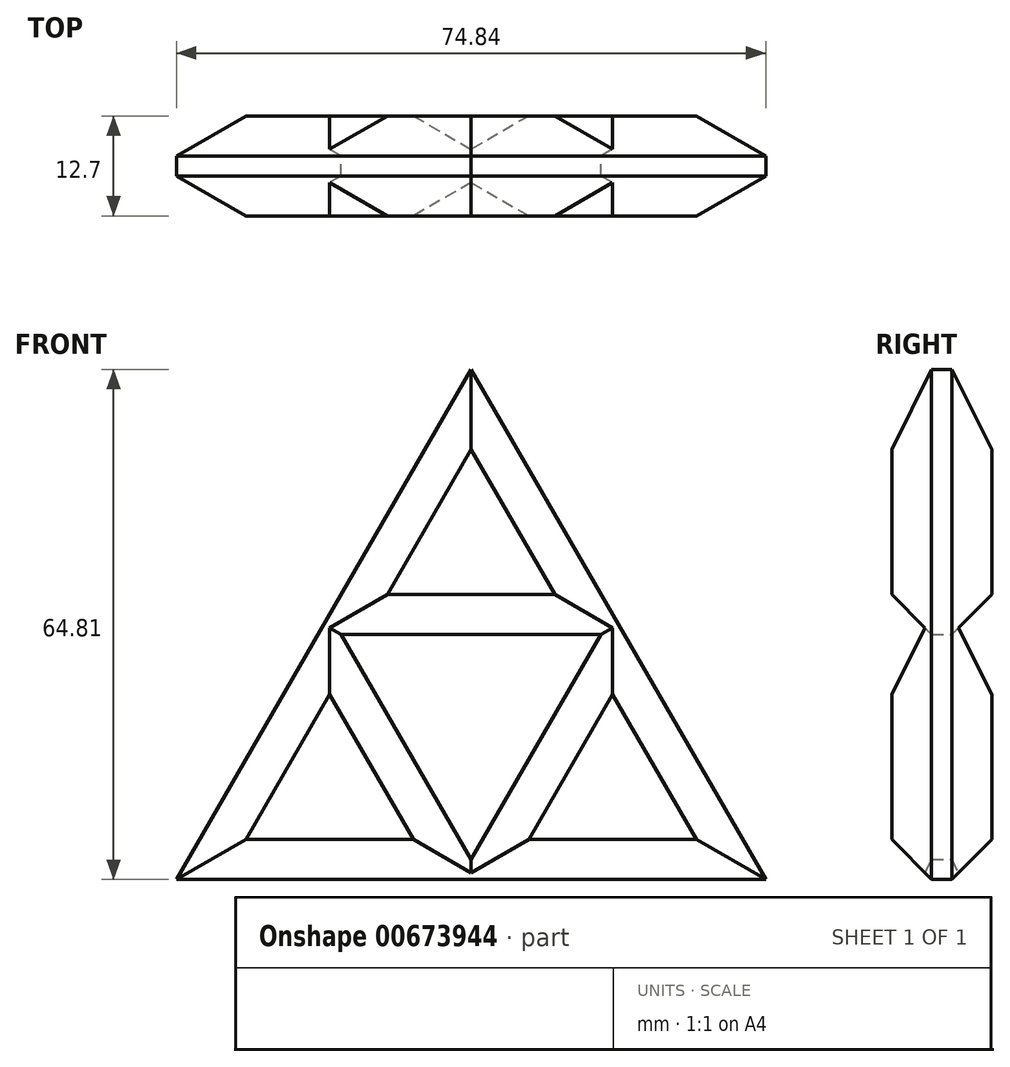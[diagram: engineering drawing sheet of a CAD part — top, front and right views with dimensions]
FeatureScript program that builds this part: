
annotation { "Feature Type Name" : "Feature", "Feature Type Description" : "" }
export const myFeature = defineFeature(function(context is Context, id is Id, definition is map)
    precondition{}
    {
        {
            var Q0;
            Q0=qCreatedBy(makeId("Front.planeOp"),FACE);
            var sketch = newSketch(context, id + "F0", { "sketchPlane" : qUnion([Q0])});
            skLineSegment(sketch, "E0", {"start": v(0, 0) * mm, "end": v(-33.02, 0) * mm});
            skLineSegment(sketch, "E1", {"start": v(-33.02, 0) * mm, "end": v(-16.51, 28.6) * mm});
            skLineSegment(sketch, "E2", {"start": v(-16.51, 28.6) * mm, "end": v(0, 0) * mm});
            skLineSegment(sketch, "E3", {"start": v(0, 0) * mm, "end": v(33.02, 0) * mm});
            skLineSegment(sketch, "E4", {"start": v(33.02, 0) * mm, "end": v(16.5, 28.6) * mm});
            skLineSegment(sketch, "E5", {"start": v(16.5, 28.6) * mm, "end": v(0, 0) * mm});
            skLineSegment(sketch, "E6", {"start": v(-16.51, 28.6) * mm, "end": v(16.5, 28.6) * mm});
            skLineSegment(sketch, "E7", {"start": v(16.51, 28.6) * mm, "end": v(0, 57.2) * mm});
            skLineSegment(sketch, "E8", {"start": v(0, 57.2) * mm, "end": v(-16.51, 28.6) * mm});
            skLineSegment(sketch, "E9", {"start": v(0, 57.2) * mm, "end": v(0, 62.27) * mm});
            skLineSegment(sketch, "E10", {"start": v(-33.02, 0) * mm, "end": v(-37.42, -2.54) * mm});
            skLineSegment(sketch, "E11", {"start": v(33.02, 0) * mm, "end": v(37.42, -2.54) * mm});
            skLineSegment(sketch, "E12", {"start": v(37.42, -2.54) * mm, "end": v(33.02, 0) * mm});
            skLineSegment(sketch, "E13", {"start": v(0, 62.27) * mm, "end": v(-37.42, -2.54) * mm});
            skLineSegment(sketch, "E14", {"start": v(-37.42, -2.54) * mm, "end": v(37.42, -2.54) * mm});
            skLineSegment(sketch, "E15", {"start": v(37.42, -2.54) * mm, "end": v(0, 62.27) * mm});
            skSolve(sketch);
        }
        {
            var Q0;
            Q0=makeQuery(id+"F0.imprint","IMPRINT",FACE,{"disambiguationData":[TD([[makeQuery(id+"F0.imprint","IMPRINT",EDGE,{"derivedFrom":sQuery(id+"F0.wireOp",EDGE,"E6")}),1.0]])]});
            var Q1;
            Q1=makeQuery(id+"F0.imprint","IMPRINT",FACE,{"disambiguationData":[TD([[makeQuery(id+"F0.imprint","IMPRINT",EDGE,{"derivedFrom":sQuery(id+"F0.wireOp",EDGE,"E0")}),-1.0]])]});
            var Q2;
            Q2=makeQuery(id+"F0.imprint","IMPRINT",FACE,{"disambiguationData":[TD([[makeQuery(id+"F0.imprint","IMPRINT",EDGE,{"derivedFrom":sQuery(id+"F0.wireOp",EDGE,"E3")}),1.0]])]});
            var Q3;
            Q3=makeQuery(id+"F0.imprint","IMPRINT",FACE,{"disambiguationData":[TD([[makeQuery(id+"F0.imprint","IMPRINT",EDGE,{"derivedFrom":sQuery(id+"F0.wireOp",EDGE,"E1")}),1.0]])]});
            var Q4;
            Q4=makeQuery(id+"F0.imprint","IMPRINT",FACE,{"disambiguationData":[TD([[makeQuery(id+"F0.imprint","IMPRINT",EDGE,{"derivedFrom":sQuery(id+"F0.wireOp",EDGE,"E4")}),-1.0]])]});
            var Q5;
            Q5=makeQuery(id+"F0.imprint","IMPRINT",FACE,{"disambiguationData":[TD([[makeQuery(id+"F0.imprint","IMPRINT",EDGE,{"derivedFrom":sQuery(id+"F0.wireOp",EDGE,"E0")}),1.0]])]});
            extrude(context, id + "F1", {"entities" : qUnion([Q0, Q1, Q2, Q3, Q4, Q5]), "depth" : 12.7 * mm});
        }
        {
            var Q0;
            Q0=makeQuery(id+"F1.opExtrude","CAP_EDGE",EDGE,{"disambiguationData":[OSD([sQuery(id+"F0.wireOp",EDGE,"E13")])],"isStart":false});
            var Q1;
            Q1=makeQuery(id+"F1.opExtrude","CAP_EDGE",EDGE,{"disambiguationData":[OSD([sQuery(id+"F0.wireOp",EDGE,"E2")])],"isStart":false});
            var Q2;
            Q2=makeQuery(id+"F1.opExtrude","CAP_EDGE",EDGE,{"disambiguationData":[OSD([sQuery(id+"F0.wireOp",EDGE,"E6")])],"isStart":false});
            var Q3;
            Q3=makeQuery(id+"F1.opExtrude","CAP_EDGE",EDGE,{"disambiguationData":[OSD([sQuery(id+"F0.wireOp",EDGE,"E5")])],"isStart":false});
            var Q4;
            Q4=makeQuery(id+"F1.opExtrude","CAP_EDGE",EDGE,{"disambiguationData":[OSD([sQuery(id+"F0.wireOp",EDGE,"E15")])],"isStart":false});
            var Q5;
            Q5=makeQuery(id+"F1.opExtrude","CAP_FACE",FACE,{"disambiguationData":[OSD([sQuery(id+"F0.wireOp",EDGE,"E2"),sQuery(id+"F0.wireOp",EDGE,"E5"),sQuery(id+"F0.wireOp",EDGE,"E6"),sQuery(id+"F0.wireOp",EDGE,"E13"),sQuery(id+"F0.wireOp",EDGE,"E14"),sQuery(id+"F0.wireOp",EDGE,"E15")])],"isStart":false});
            var Q6;
            Q6=makeQuery(id+"F1.opExtrude","CAP_EDGE",EDGE,{"disambiguationData":[OSD([sQuery(id+"F0.wireOp",EDGE,"E13")])],"isStart":true});
            var Q7;
            Q7=makeQuery(id+"F1.opExtrude","CAP_EDGE",EDGE,{"disambiguationData":[OSD([sQuery(id+"F0.wireOp",EDGE,"E15")])],"isStart":true});
            var Q8;
            Q8=makeQuery(id+"F1.opExtrude","CAP_EDGE",EDGE,{"disambiguationData":[OSD([sQuery(id+"F0.wireOp",EDGE,"E14")])],"isStart":true});
            var Q9;
            Q9=makeQuery(id+"F1.opExtrude","CAP_EDGE",EDGE,{"disambiguationData":[OSD([sQuery(id+"F0.wireOp",EDGE,"E5")])],"isStart":true});
            var Q10;
            Q10=makeQuery(id+"F1.opExtrude","CAP_EDGE",EDGE,{"disambiguationData":[OSD([sQuery(id+"F0.wireOp",EDGE,"E6")])],"isStart":true});
            var Q11;
            Q11=makeQuery(id+"F1.opExtrude","CAP_EDGE",EDGE,{"disambiguationData":[OSD([sQuery(id+"F0.wireOp",EDGE,"E2")])],"isStart":true});
            chamfer(context, id + "F2", {"entities" : qUnion([Q0, Q1, Q2, Q3, Q4, Q5, Q6, Q7, Q8, Q9, Q10, Q11]), "width" : 5.08 * mm, "tangentPropagation" : true});
        }
        {
            var Q0;
            Q0=makeQuery(id+"F2.opChamfer","SPLIT",FACE,{"disambiguationData":[OD(0.0)],"derivedFrom":makeQuery(id+"F1.opExtrude","CAP_FACE",FACE,{"disambiguationData":[OSD([sQuery(id+"F0.wireOp",EDGE,"E2"),sQuery(id+"F0.wireOp",EDGE,"E5"),sQuery(id+"F0.wireOp",EDGE,"E6"),sQuery(id+"F0.wireOp",EDGE,"E13"),sQuery(id+"F0.wireOp",EDGE,"E14"),sQuery(id+"F0.wireOp",EDGE,"E15")])],"isStart":false})});
            var Q1;
            {var subQ0=sQuery(id+"F0.wireOp",EDGE,"E2");Q1=makeQuery(id+"F2.opChamfer","BLEND_FACE",FACE,{"disambiguationData":[OSD([subQ0]),TDD([makeQuery(id+"F1.opExtrude","CAP_EDGE",EDGE,{"disambiguationData":[OSD([subQ0])],"isStart":false})])]});}
            var Q2;
            {var subQ0=sQuery(id+"F0.wireOp",EDGE,"E6");Q2=makeQuery(id+"F2.opChamfer","BLEND_FACE",FACE,{"disambiguationData":[OSD([subQ0]),TDD([makeQuery(id+"F1.opExtrude","CAP_EDGE",EDGE,{"disambiguationData":[OSD([subQ0])],"isStart":false})])]});}
            var Q3;
            Q3=makeQuery(id+"F2.opChamfer","SPLIT",FACE,{"disambiguationData":[OD(2.0)],"derivedFrom":makeQuery(id+"F1.opExtrude","CAP_FACE",FACE,{"disambiguationData":[OSD([sQuery(id+"F0.wireOp",EDGE,"E2"),sQuery(id+"F0.wireOp",EDGE,"E5"),sQuery(id+"F0.wireOp",EDGE,"E6"),sQuery(id+"F0.wireOp",EDGE,"E13"),sQuery(id+"F0.wireOp",EDGE,"E14"),sQuery(id+"F0.wireOp",EDGE,"E15")])],"isStart":false})});
            var Q4;
            {var subQ0=sQuery(id+"F0.wireOp",EDGE,"E5");Q4=makeQuery(id+"F2.opChamfer","BLEND_FACE",FACE,{"disambiguationData":[OSD([subQ0]),TDD([makeQuery(id+"F1.opExtrude","CAP_EDGE",EDGE,{"disambiguationData":[OSD([subQ0])],"isStart":false})])]});}
            var Q5;
            Q5=makeQuery(id+"F2.opChamfer","SPLIT",FACE,{"disambiguationData":[OD(1.0)],"derivedFrom":makeQuery(id+"F1.opExtrude","CAP_FACE",FACE,{"disambiguationData":[OSD([sQuery(id+"F0.wireOp",EDGE,"E2"),sQuery(id+"F0.wireOp",EDGE,"E5"),sQuery(id+"F0.wireOp",EDGE,"E6"),sQuery(id+"F0.wireOp",EDGE,"E13"),sQuery(id+"F0.wireOp",EDGE,"E14"),sQuery(id+"F0.wireOp",EDGE,"E15")])],"isStart":false})});
            var Q6;
            {var subQ0=sQuery(id+"F0.wireOp",EDGE,"E14");Q6=makeQuery(id+"F2.opChamfer","BLEND_FACE",FACE,{"disambiguationData":[OSD([subQ0]),TDD([makeQuery(id+"F1.opExtrude","CAP_EDGE",EDGE,{"disambiguationData":[OSD([subQ0])],"isStart":false})])]});}
            var Q7;
            {var subQ0=sQuery(id+"F0.wireOp",EDGE,"E15");Q7=makeQuery(id+"F2.opChamfer","BLEND_FACE",FACE,{"disambiguationData":[OSD([subQ0]),TDD([makeQuery(id+"F1.opExtrude","CAP_EDGE",EDGE,{"disambiguationData":[OSD([subQ0])],"isStart":false})])]});}
            var Q8;
            {var subQ0=sQuery(id+"F0.wireOp",EDGE,"E13");Q8=makeQuery(id+"F2.opChamfer","BLEND_FACE",FACE,{"disambiguationData":[OSD([subQ0]),TDD([makeQuery(id+"F1.opExtrude","CAP_EDGE",EDGE,{"disambiguationData":[OSD([subQ0])],"isStart":false})])]});}
            extrude(context, id + "F3", {"entities" : qUnion([Q0, Q1, Q2, Q3, Q4, Q5, Q6, Q7, Q8]), "operationType" : NewBodyOperationType.REMOVE, "oppositeDirection" : true, "depth" : 2.3 * mm});
        }
        {
            var Q0;
            {var subQ0=sQuery(id+"F0.wireOp",EDGE,"E15");var subQ1=sQuery(id+"F0.wireOp",EDGE,"E14");var subQ2=sQuery(id+"F0.wireOp",EDGE,"E13");var subQ3=sQuery(id+"F0.wireOp",EDGE,"E6");var subQ4=sQuery(id+"F0.wireOp",EDGE,"E5");var subQ5=sQuery(id+"F0.wireOp",EDGE,"E2");Q0=makeQuery(id+"F3.boolean.opBoolean","COPY",FACE,{"derivedFrom":makeQuery(id+"F3.opExtrude","CAP_FACE",FACE,{"disambiguationData":[OSD([subQ5,subQ4,subQ3,subQ2,subQ1,subQ0]),TDD([makeQuery(id+"F2.opChamfer","SPLIT",FACE,{"disambiguationData":[OD(0.0)],"derivedFrom":makeQuery(id+"F1.opExtrude","CAP_FACE",FACE,{"disambiguationData":[OSD([subQ5,subQ4,subQ3,subQ2,subQ1,subQ0])],"isStart":false})})])],"isStart":false})});}
            var Q1;
            {var subQ0=sQuery(id+"F0.wireOp",EDGE,"E15");var subQ1=sQuery(id+"F0.wireOp",EDGE,"E14");var subQ2=sQuery(id+"F0.wireOp",EDGE,"E13");var subQ3=sQuery(id+"F0.wireOp",EDGE,"E6");var subQ4=sQuery(id+"F0.wireOp",EDGE,"E5");var subQ5=sQuery(id+"F0.wireOp",EDGE,"E2");Q1=makeQuery(id+"F3.boolean.opBoolean","COPY",FACE,{"derivedFrom":makeQuery(id+"F3.opExtrude","CAP_FACE",FACE,{"disambiguationData":[OSD([subQ5,subQ4,subQ3,subQ2,subQ1,subQ0]),TDD([makeQuery(id+"F2.opChamfer","SPLIT",FACE,{"disambiguationData":[OD(2.0)],"derivedFrom":makeQuery(id+"F1.opExtrude","CAP_FACE",FACE,{"disambiguationData":[OSD([subQ5,subQ4,subQ3,subQ2,subQ1,subQ0])],"isStart":false})})])],"isStart":false})});}
            var Q2;
            Q2=makeQuery(id+"F3.boolean.opBoolean","COPY",FACE,{"derivedFrom":makeQuery(id+"F3.opExtrude","CAP_FACE",FACE,{"disambiguationData":[OSD([sQuery(id+"F0.wireOp",EDGE,"E13")]),OD(1.0)],"isStart":false})});
            var Q3;
            {var subQ0=sQuery(id+"F0.wireOp",EDGE,"E15");var subQ1=sQuery(id+"F0.wireOp",EDGE,"E14");var subQ2=sQuery(id+"F0.wireOp",EDGE,"E13");var subQ3=sQuery(id+"F0.wireOp",EDGE,"E6");var subQ4=sQuery(id+"F0.wireOp",EDGE,"E5");var subQ5=sQuery(id+"F0.wireOp",EDGE,"E2");Q3=makeQuery(id+"F3.boolean.opBoolean","COPY",FACE,{"derivedFrom":makeQuery(id+"F3.opExtrude","CAP_FACE",FACE,{"disambiguationData":[OSD([subQ5,subQ4,subQ3,subQ2,subQ1,subQ0]),TDD([makeQuery(id+"F2.opChamfer","SPLIT",FACE,{"disambiguationData":[OD(1.0)],"derivedFrom":makeQuery(id+"F1.opExtrude","CAP_FACE",FACE,{"disambiguationData":[OSD([subQ5,subQ4,subQ3,subQ2,subQ1,subQ0])],"isStart":false})})])],"isStart":false})});}
            var Q4;
            Q4=makeQuery(id+"F3.boolean.opBoolean","COPY",FACE,{"derivedFrom":makeQuery(id+"F3.opExtrude","CAP_FACE",FACE,{"disambiguationData":[OSD([sQuery(id+"F0.wireOp",EDGE,"E14")]),OD(1.0)],"isStart":false})});
            var Q5;
            Q5=makeQuery(id+"F3.boolean.opBoolean","COPY",FACE,{"derivedFrom":makeQuery(id+"F3.opExtrude","CAP_FACE",FACE,{"disambiguationData":[OSD([sQuery(id+"F0.wireOp",EDGE,"E2")]),OD(1.0)],"isStart":false})});
            var Q6;
            Q6=makeQuery(id+"F3.boolean.opBoolean","COPY",FACE,{"derivedFrom":makeQuery(id+"F3.opExtrude","CAP_FACE",FACE,{"disambiguationData":[OSD([sQuery(id+"F0.wireOp",EDGE,"E6")]),OD(1.0)],"isStart":false})});
            var Q7;
            Q7=makeQuery(id+"F3.boolean.opBoolean","COPY",FACE,{"derivedFrom":makeQuery(id+"F3.opExtrude","CAP_FACE",FACE,{"disambiguationData":[OSD([sQuery(id+"F0.wireOp",EDGE,"E5")]),OD(1.0)],"isStart":false})});
            var Q8;
            Q8=makeQuery(id+"F3.boolean.opBoolean","COPY",FACE,{"derivedFrom":makeQuery(id+"F3.opExtrude","CAP_FACE",FACE,{"disambiguationData":[OSD([sQuery(id+"F0.wireOp",EDGE,"E15")]),OD(1.0)],"isStart":false})});
            extrude(context, id + "F4", {"entities" : qUnion([Q0, Q1, Q2, Q3, Q4, Q5, Q6, Q7, Q8]), "operationType" : NewBodyOperationType.ADD, "depth" : 2.3 * mm});
        }
    });
